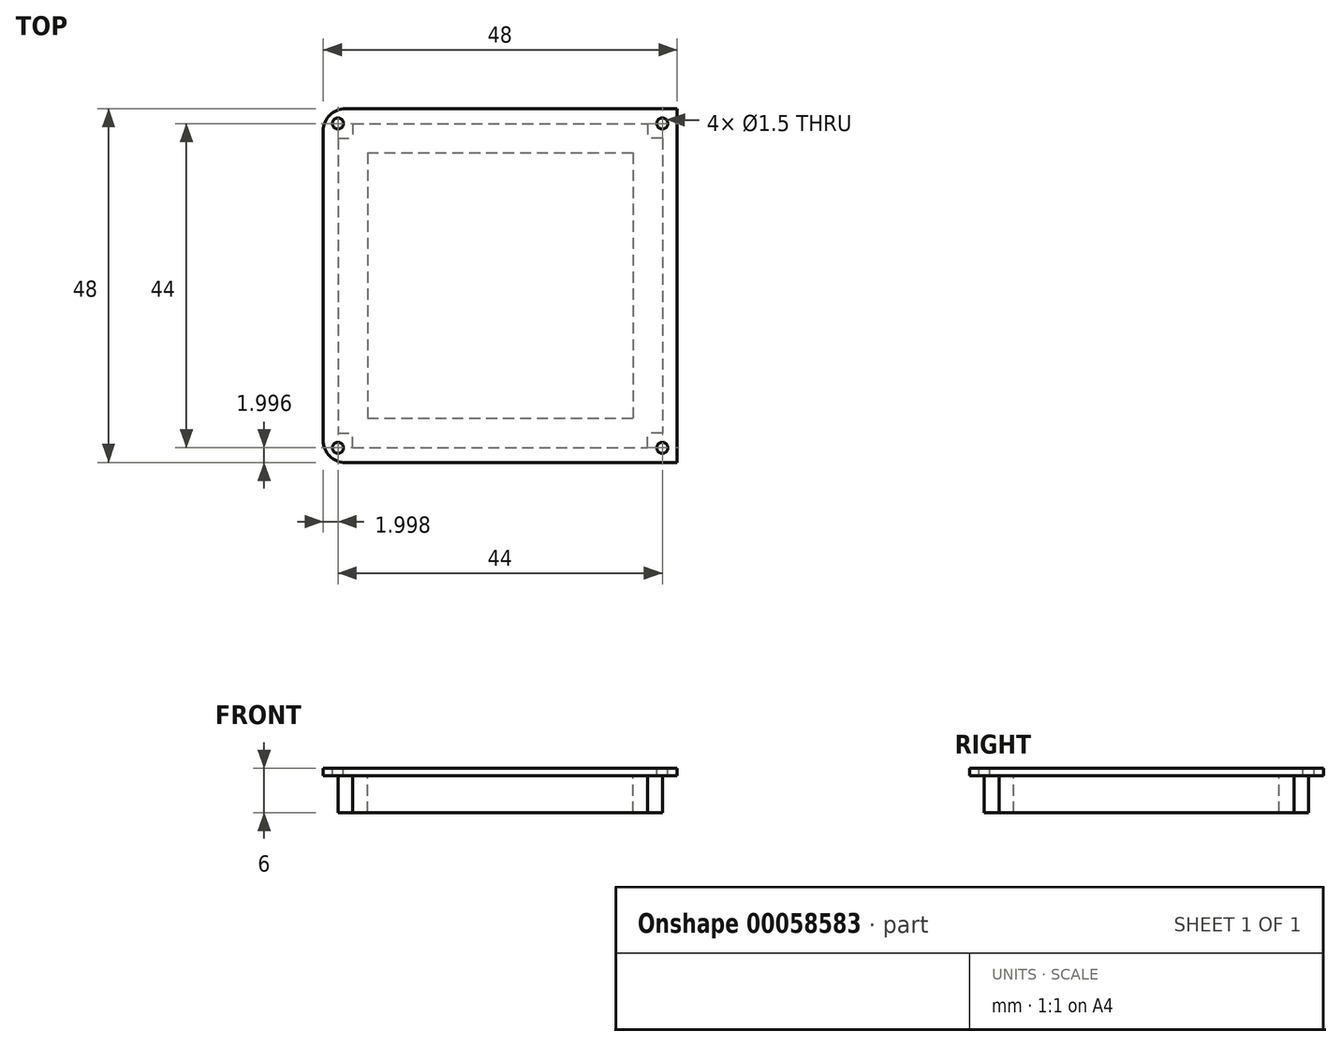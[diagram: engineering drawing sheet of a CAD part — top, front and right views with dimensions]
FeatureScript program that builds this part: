
annotation { "Feature Type Name" : "Feature", "Feature Type Description" : "" }
export const myFeature = defineFeature(function(context is Context, id is Id, definition is map)
    precondition{}
    {
        {
            var Q0;
            Q0=qCreatedBy(makeId("Top.planeOp"),FACE);
            var sketch = newSketch(context, id + "F0", { "sketchPlane" : qUnion([Q0])});
            skLineSegment(sketch, "E0.0.0", {"start": v(23.15, -25) * mm, "end": v(23.15, 23) * mm});
            skLineSegment(sketch, "E0.0.1", {"start": v(23.15, 23) * mm, "end": v(-24.85, 23) * mm});
            skLineSegment(sketch, "E0.0.2", {"start": v(-24.85, 23) * mm, "end": v(-24.85, -25) * mm});
            skLineSegment(sketch, "E0.0.3", {"start": v(-24.85, -25) * mm, "end": v(23.15, -25) * mm});
            skLineSegment(sketch, "E1.0.0", {"start": v(21.15, 19) * mm, "end": v(19.15, 19) * mm});
            skLineSegment(sketch, "E1.0.1", {"start": v(19.15, 19) * mm, "end": v(19.15, 21) * mm});
            skLineSegment(sketch, "E1.0.2", {"start": v(19.15, 21) * mm, "end": v(-20.85, 21) * mm});
            skLineSegment(sketch, "E1.0.3", {"start": v(-20.85, 21) * mm, "end": v(-20.85, 19) * mm});
            skLineSegment(sketch, "E1.0.4", {"start": v(-20.85, 19) * mm, "end": v(-22.85, 19) * mm});
            skLineSegment(sketch, "E1.0.5", {"start": v(-22.85, 19) * mm, "end": v(-22.85, -21) * mm});
            skLineSegment(sketch, "E1.0.6", {"start": v(-22.85, -21) * mm, "end": v(-20.85, -21) * mm});
            skLineSegment(sketch, "E1.0.7", {"start": v(-20.85, -21) * mm, "end": v(-20.85, -23) * mm});
            skLineSegment(sketch, "E1.0.8", {"start": v(-20.85, -23) * mm, "end": v(19.15, -23) * mm});
            skLineSegment(sketch, "E1.0.9", {"start": v(19.15, -23) * mm, "end": v(19.15, -21) * mm});
            skLineSegment(sketch, "E1.0.10", {"start": v(19.15, -21) * mm, "end": v(21.15, -21) * mm});
            skLineSegment(sketch, "E1.0.11", {"start": v(21.15, -21) * mm, "end": v(21.15, 19) * mm});
            skSolve(sketch);
        }
        {
            var Q0;
            Q0=makeQuery(id+"F0.imprint","IMPRINT",FACE,{"disambiguationData":[TD([[makeQuery(id+"F0.imprint","IMPRINT",EDGE,{"derivedFrom":sQuery(id+"F0.wireOp",EDGE,"E0.0.0")}),1.0]])]});
            var Q1;
            Q1=makeQuery(id+"F0.imprint","IMPRINT",FACE,{"disambiguationData":[TD([[makeQuery(id+"F0.imprint","IMPRINT",EDGE,{"derivedFrom":sQuery(id+"F0.wireOp",EDGE,"E1.0.0")}),1.0]])]});
            var Q2;
            Q2=sQuery(id+"F0.wireOp",EDGE,"E0.0.0");
            var Q3;
            Q3=sQuery(id+"F0.wireOp",EDGE,"E0.0.1");
            var Q4;
            Q4=sQuery(id+"F0.wireOp",EDGE,"E0.0.2");
            var Q5;
            Q5=sQuery(id+"F0.wireOp",EDGE,"E0.0.3");
            var Q6;
            Q6=sQuery(id+"F0.wireOp",EDGE,"E1.0.0");
            var Q7;
            Q7=sQuery(id+"F0.wireOp",EDGE,"E1.0.1");
            var Q8;
            Q8=sQuery(id+"F0.wireOp",EDGE,"E1.0.2");
            var Q9;
            Q9=sQuery(id+"F0.wireOp",EDGE,"E1.0.3");
            var Q10;
            Q10=sQuery(id+"F0.wireOp",EDGE,"E1.0.4");
            var Q11;
            Q11=sQuery(id+"F0.wireOp",EDGE,"E1.0.5");
            var Q12;
            Q12=sQuery(id+"F0.wireOp",EDGE,"E1.0.6");
            var Q13;
            Q13=sQuery(id+"F0.wireOp",EDGE,"E1.0.7");
            var Q14;
            Q14=sQuery(id+"F0.wireOp",EDGE,"E1.0.8");
            var Q15;
            Q15=sQuery(id+"F0.wireOp",EDGE,"E1.0.9");
            var Q16;
            Q16=sQuery(id+"F0.wireOp",EDGE,"E1.0.10");
            var Q17;
            Q17=sQuery(id+"F0.wireOp",EDGE,"E1.0.11");
            extrude(context, id + "F1", {"entities" : qUnion([Q0, Q1]), "surfaceEntities" : qUnion([Q2, Q3, Q4, Q5, Q6, Q7, Q8, Q9, Q10, Q11, Q12, Q13, Q14, Q15, Q16, Q17]), "depth" : 1 * mm});
        }
        {
            var Q0;
            Q0=qCreatedBy(makeId("Top.planeOp"),FACE);
            var sketch = newSketch(context, id + "F2", { "sketchPlane" : qUnion([Q0])});
            skPoint(sketch, "E2.0", {"position": v(-20.85, 21) * mm});
            skPoint(sketch, "E3.0", {"position": v(-22.85, 19) * mm});
            skPoint(sketch, "E4.0", {"position": v(-20.85, -23) * mm});
            skPoint(sketch, "E5.0", {"position": v(21.15, -21) * mm});
            skPoint(sketch, "E6.0", {"position": v(19.15, 21) * mm});
            skPoint(sketch, "E7.0", {"position": v(21.15, 19) * mm});
            skPoint(sketch, "E8.0", {"position": v(-22.85, -21) * mm});
            skPoint(sketch, "E9.0", {"position": v(19.15, -23) * mm});
            skLineSegment(sketch, "E10.bottom", {"start": v(-20.85, -23) * mm, "end": v(19.15, -23) * mm});
            skLineSegment(sketch, "E10.top", {"start": v(-20.85, -19) * mm, "end": v(19.15, -19) * mm});
            skLineSegment(sketch, "E10.left", {"start": v(-20.85, -23) * mm, "end": v(-20.85, -19) * mm});
            skLineSegment(sketch, "E10.right", {"start": v(19.15, -23) * mm, "end": v(19.15, -19) * mm});
            skLineSegment(sketch, "E11.bottom", {"start": v(-22.85, 19) * mm, "end": v(-18.85, 19) * mm});
            skLineSegment(sketch, "E11.top", {"start": v(-22.85, -21) * mm, "end": v(-18.85, -21) * mm});
            skLineSegment(sketch, "E11.left", {"start": v(-22.85, 19) * mm, "end": v(-22.85, -21) * mm});
            skLineSegment(sketch, "E11.right", {"start": v(-18.85, 19) * mm, "end": v(-18.85, -21) * mm});
            skLineSegment(sketch, "E12.bottom", {"start": v(-20.85, 21) * mm, "end": v(19.15, 21) * mm});
            skLineSegment(sketch, "E12.top", {"start": v(-20.85, 17) * mm, "end": v(19.15, 17) * mm});
            skLineSegment(sketch, "E12.left", {"start": v(-20.85, 21) * mm, "end": v(-20.85, 17) * mm});
            skLineSegment(sketch, "E12.right", {"start": v(19.15, 21) * mm, "end": v(19.15, 17) * mm});
            skLineSegment(sketch, "E13.bottom", {"start": v(21.15, 19) * mm, "end": v(17.15, 19) * mm});
            skLineSegment(sketch, "E13.top", {"start": v(21.15, -21) * mm, "end": v(17.15, -21) * mm});
            skLineSegment(sketch, "E13.left", {"start": v(21.15, 19) * mm, "end": v(21.15, -21) * mm});
            skLineSegment(sketch, "E13.right", {"start": v(17.15, 19) * mm, "end": v(17.15, -21) * mm});
            skSolve(sketch);
        }
        {
            var Q0;
            Q0 = qSketchRegion(id + "F2", true);
            extrude(context, id + "F3", {"entities" : qUnion([Q0]), "operationType" : NewBodyOperationType.ADD, "oppositeDirection" : true, "depth" : 5 * mm});
        }
        {
            var Q0;
            Q0=makeQuery(id+"F1.opExtrude","CAP_FACE",FACE,{"disambiguationData":[OSD([sQuery(id+"F0.wireOp",EDGE,"E0.0.0"),sQuery(id+"F0.wireOp",EDGE,"E0.0.1"),sQuery(id+"F0.wireOp",EDGE,"E0.0.2"),sQuery(id+"F0.wireOp",EDGE,"E0.0.3")])],"isStart":false});
            var sketch = newSketch(context, id + "F4", { "sketchPlane" : qUnion([Q0])});
            skLineSegment(sketch, "E14.0", {"start": v(-22.85, -23) * mm, "end": v(21.15, -23) * mm, "construction": true});
            skLineSegment(sketch, "E14.1", {"start": v(-22.85, 21) * mm, "end": v(-22.85, -23) * mm, "construction": true});
            skLineSegment(sketch, "E14.2", {"start": v(21.15, 21) * mm, "end": v(-22.85, 21) * mm, "construction": true});
            skLineSegment(sketch, "E14.3", {"start": v(21.15, -23) * mm, "end": v(21.15, 21) * mm, "construction": true});
            skPoint(sketch, "E15", {"position": v(-22.85, 21) * mm});
            skPoint(sketch, "E16", {"position": v(-22.85, -23) * mm});
            skPoint(sketch, "E17", {"position": v(21.15, -23) * mm});
            skPoint(sketch, "E18", {"position": v(21.15, 21) * mm});
            skSolve(sketch);
        }
        {
            var Q0;
            Q0=sQuery(id+"F4.wireOp",VERTEX,"E15");
            var Q1;
            Q1=sQuery(id+"F4.wireOp",VERTEX,"E16");
            var Q2;
            Q2=sQuery(id+"F4.wireOp",VERTEX,"E17");
            var Q3;
            Q3=sQuery(id+"F4.wireOp",VERTEX,"E18");
            var Q4;
            Q4=makeQuery(id+"F1.opExtrude","SWEPT_BODY",BODY,{"disambiguationData":[OSD([sQuery(id+"F0.wireOp",EDGE,"E0.0.0"),sQuery(id+"F0.wireOp",EDGE,"E0.0.1"),sQuery(id+"F0.wireOp",EDGE,"E0.0.2"),sQuery(id+"F0.wireOp",EDGE,"E0.0.3")])]});
            hole(context, id + "F5", {"style" : HoleStyle.SIMPLE, "holeDiameter" : 1.5 * mm, "endStyle" : HoleEndStyle.THROUGH, "locations" : qUnion([Q0, Q1, Q2, Q3]), "scope" : qUnion([Q4])});
        }
        {
            var Q0;
            Q0=makeQuery(id+"F1.opExtrude","SWEPT_EDGE",EDGE,{"disambiguationData":[OSD([sQuery(id+"F0.wireOp",EDGE,"E0.0.2"),sQuery(id+"F0.wireOp",EDGE,"E0.0.3")])]});
            var Q1;
            Q1=makeQuery(id+"F1.opExtrude","SWEPT_EDGE",EDGE,{"disambiguationData":[OSD([sQuery(id+"F0.wireOp",EDGE,"E0.0.1"),sQuery(id+"F0.wireOp",EDGE,"E0.0.2")])]});
            fillet(context, id + "F6", {"entities" : qUnion([Q0, Q1]), "radius" : 3 * mm, "tangentPropagation" : true, "allowEdgeOverflow" : false});
        }
    });
